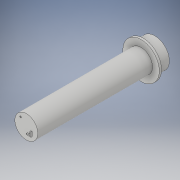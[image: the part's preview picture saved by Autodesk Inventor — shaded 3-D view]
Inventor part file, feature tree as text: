
AUTODESK INVENTOR PART (.ipt)
format: ipt  version: 2019 (Build 230136000, 136)  size: 135,168 bytes
history: native  units: in
note: dims shown in document units (in); Inventor stores cm internally (conversion verified against a paired STEP export)
features: extrude x4, sketch x4, hole x1
ambient origin geometry x8: Origin, YZ Plane, XZ Plane, XY Plane, X Axis, Y Axis, Z Axis, Center Point
bodies: Solid1 (feature_tree)
feature tree (9):
  extrude  "Extrusion1"  Depth=0.0787in TaperAngle=0.0deg
  extrude  "Extrusion8"  Depth=0.0394in
  sketch  "Sketch4"  dims[d16=0.315in d17=0.0394in]
  extrude  "Extrusion6"  Depth=0.1575in
  extrude  "Extrusion7"  Depth=3.937in
  hole  "Hole4"  [1 undecoded]
  sketch  "Sketch1"  dims[d0=1.5748in d1=0.0787in d2=0.0in]
  sketch  "Sketch9"  dims[d18=0.1575in d30=0.1969in]
  sketch  "Sketch10"  dims[d31=0.1969in d51=1.25in d52=1.0in d53=0.3937in d54=0.0in d55=0.0394in d56=0.0in d57=0.0561in d58=0.146in d59=0.1575in d60=0.0787in d61=90.0deg d62=0.2241in d63=0.8108in d64=0.7874in d65=3.937in d66=0.0in]
note: 1 required parameter value undecoded (feature->parameter linkage not recoverable at this tier; creation-order binding heuristic only, values carry confidence <= 0.55)
